# Revit family: Door_Raised-Panel
name_source: partatom
category: Doors
units: mm (PartAtom-declared; Revit-internal decimal feet)

## family parameters
Always vertical = Yes
Classification Number = 23.30.10.11.17
Cut with Voids When Loaded = No
Host = Wall
Room Calculation Point = No
Shared = No

## types (18) — shared parameters
Assembly Code = C1020100
Building Codes = http://www.iccsafe.org
CasingMaterial = ARCAT - Wood - Cherry_Domestic
CladdingMaterial = ARCAT - Metal - Aluminum_0.032" - Burgundy
Construction Details = http://www.arcat.com
ENERGYSTAR Rating = North/Central
Expected Lifespan (Years) = 15
Fax = (203) 929-2444
Fire Rating = 1 hour
Function = Interior
Green Building-LEED = http://www.arcat.com
HandleHeight = 3' - 0"
JambMaterial = ARCAT - Wood - Pine_Northern White
JambThickness = 0' - 0 3/4"
Keynote = 08200
LateralClearance = 0' - 1 1/2"
Maintenance Schedule (Months) = 36
Manufacturer = Generic
Model = Generic
PanelCheck = 4
PanelThickness = 0' - 0 27/32"
PnViz2 = Yes
PnViz3 = Yes
PnViz4 = No
Product Data = http://www.arcat.com
Product Properties = http://www.arcat.com
Rail-Bottom = 1' - 0"
Rail-Center = 0' - 6"
Rail-Top = 0' - 8"
Raised Panel Count = 4
Rough Opening Clearance = 0' - 0 3/4"
SHGC = 0.54
SlabMaterial = ARCAT - Wood - Pine_Northern White
SlabThickness = 0' - 2 1/2"
Specification = http://www.arcat.com
Test Data = http://www.aamanet.org
Thickness = 0' - 2 1/2"
URL = http://www.arcat.com
U_Factor = 0.39
Usage = Interior
Wall Closure = By host
Warranty Duration (Years) = 10
zero-valued in all types: R_Value

## per-type parameters (varying)
| type | Description | Height | Rough Height | Rough Width | Stile | Width |
| 3-0 x 8-0 | 3-0 x 8-0 Raised Panel Interior Door | 8' - 0" | 8' - 1 1/2" | 3' - 3" | 0' - 4" | 3' - 0" |
| 3-0 x 7-6 | 3-0 x 7-6 Raised Panel Interior Door | 7' - 6" | 7' - 7 1/2" | 3' - 3" | 0' - 4" | 3' - 0" |
| 3-0 x 6-8 | 3-0 x 6-8 Raised Panel Interior Door | 6' - 8" | 6' - 9 1/2" | 3' - 3" | 0' - 4" | 3' - 0" |
| 2-8 x 8-0 | 2-8 x 8-0 Raised Panel Interior Door | 8' - 0" | 8' - 1 1/2" | 2' - 11" | 0' - 4" | 2' - 8" |
| 2-8 x 7-6 | 2-8 x 7-6 Raised Panel Interior Door | 7' - 6" | 7' - 7 1/2" | 2' - 11" | 0' - 4" | 2' - 8" |
| 2-8 x 6-8 | 2-8 x 6-8 Raised Panel Interior Door | 6' - 8" | 6' - 9 1/2" | 2' - 11" | 0' - 4" | 2' - 8" |
| 2-6 x 8-0 | 2-6 x 8-0 Raised Panel Interior Door | 8' - 0" | 8' - 1 1/2" | 2' - 9" | 0' - 4" | 2' - 6" |
| 2-6 x 7-6 | 2-6 x 7-6 Raised Panel Interior Door | 7' - 6" | 7' - 7 1/2" | 2' - 9" | 0' - 4" | 2' - 6" |
| 2-6 x 6-8 | 2-6 x 6-8 Raised Panel Interior Door | 6' - 8" | 6' - 9 1/2" | 2' - 9" | 0' - 4" | 2' - 6" |
| 2-4 x 8-0 | 2-4 x 8-0 Raised Panel Interior Door | 8' - 0" | 8' - 1 1/2" | 2' - 7" | 0' - 4" | 2' - 4" |
| 2-4 x 7-6 | 2-4 x 7-6 Raised Panel Interior Door | 7' - 6" | 7' - 7 1/2" | 2' - 7" | 0' - 4" | 2' - 4" |
| 2-4 x 6-8 | 2-4 x 6-8 Raised Panel Interior Door | 6' - 8" | 6' - 9 1/2" | 2' - 7" | 0' - 4" | 2' - 4" |
| 2-0 x 8-0 | 2-0 x 8-0 Raised Panel Interior Door | 8' - 0" | 8' - 1 1/2" | 2' - 3" | 0' - 4" | 2' - 0" |
| 2-0 x 7-6 | 2-0 x 7-6 Raised Panel Interior Door | 7' - 6" | 7' - 7 1/2" | 2' - 3" | 0' - 4" | 2' - 0" |
| 2-0 x 6-8 | 2-0 x 6-8 Raised Panel Interior Door | 6' - 8" | 6' - 9 1/2" | 2' - 3" | 0' - 4" | 2' - 0" |
| 1-8 x 8-0 | 1-8 x 8-0 Raised Panel Interior Door | 8' - 0" | 8' - 1 1/2" | 1' - 11" | 0' - 3" | 1' - 8" |
| 1-8 x 7-6 | 1-8 x 7-6 Raised Panel Interior Door | 7' - 6" | 7' - 7 1/2" | 1' - 11" | 0' - 3" | 1' - 8" |
| 1-8 x 6-8 | 1-8 x 6-8 Raised Panel Interior Door | 6' - 8" | 6' - 9 1/2" | 1' - 11" | 0' - 3" | 1' - 8" |

## geometry (parser evidence)
native form markers: Sweep x9
no freeform markers — native parametric forms only
